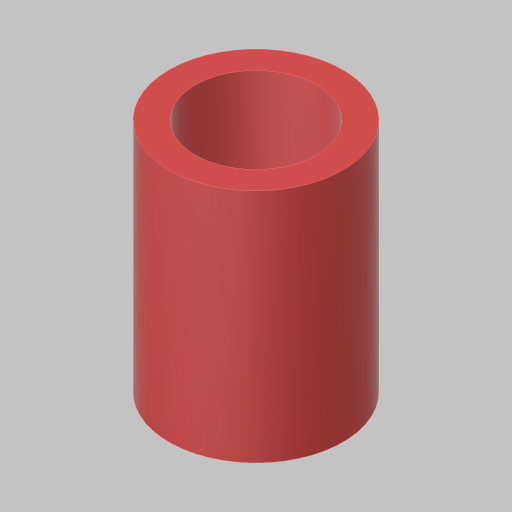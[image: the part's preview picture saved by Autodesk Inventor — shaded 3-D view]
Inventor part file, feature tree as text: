
AUTODESK INVENTOR PART (.ipt)
format: ipt  version: 2023.5 (Build 275446000, 446)  size: 112,640 bytes
history: native  units: in
note: dims shown in document units (in); Inventor stores cm internally (conversion verified against a paired STEP export)
features: extrude x1, sketch x1
ambient origin geometry x8: Origin, YZ Plane, XZ Plane, XY Plane, X Axis, Y Axis, Z Axis, Center Point
bodies: Solid1 (feature_tree)
feature tree (2):
  extrude  "Extrusion1"  Depth=1.125in
  sketch  "Sketch1"  dims[d0=0.58in d1=0.125in d2=1.125in d3=0.0in]
